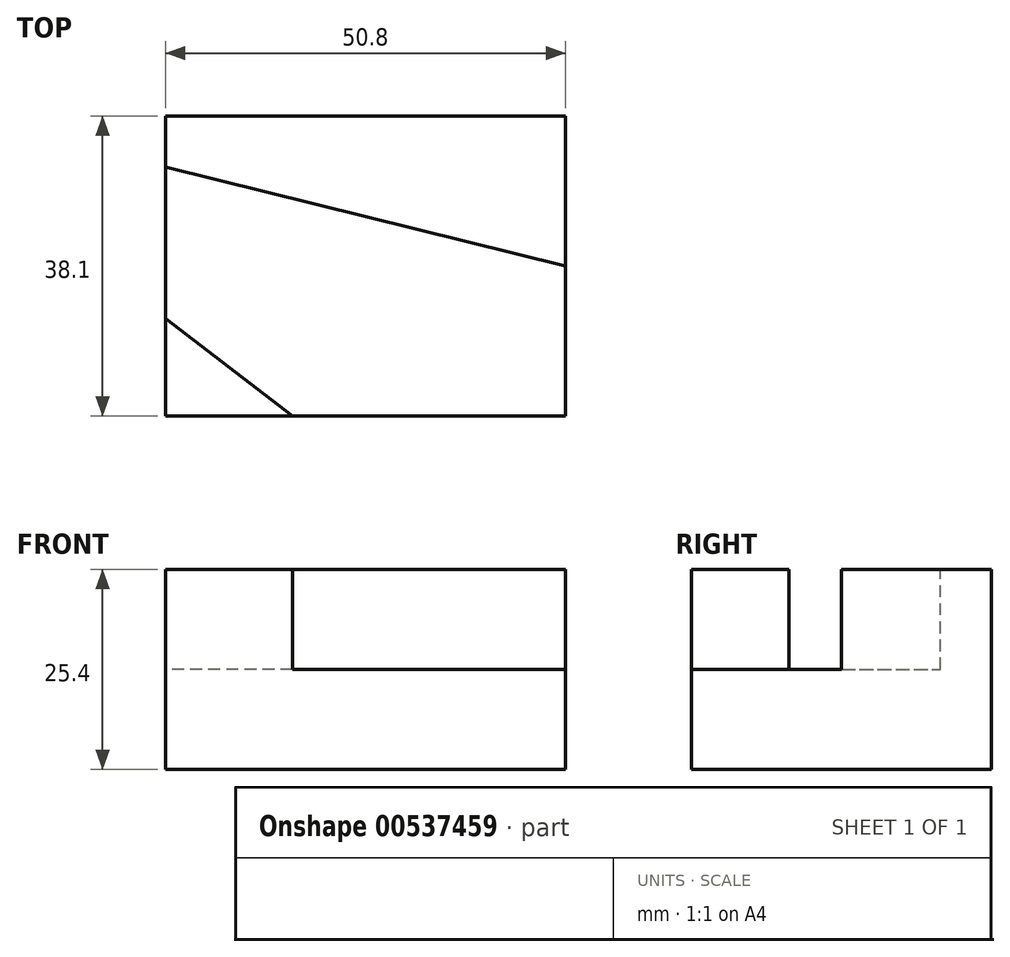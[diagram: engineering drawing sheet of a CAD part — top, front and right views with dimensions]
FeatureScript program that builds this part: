
annotation { "Feature Type Name" : "Feature", "Feature Type Description" : "" }
export const myFeature = defineFeature(function(context is Context, id is Id, definition is map)
    precondition{}
    {
        {
            var Q0;
            Q0=qCreatedBy(makeId("Right.planeOp"),FACE);
            var sketch = newSketch(context, id + "F0", { "sketchPlane" : qUnion([Q0])});
            skLineSegment(sketch, "E0", {"start": v(0, 0) * mm, "end": v(0, 25.4) * mm});
            skLineSegment(sketch, "E1", {"start": v(0, 25.4) * mm, "end": v(38.1, 25.4) * mm});
            skLineSegment(sketch, "E2", {"start": v(38.1, 25.4) * mm, "end": v(38.1, 0) * mm});
            skLineSegment(sketch, "E3", {"start": v(38.1, 0) * mm, "end": v(0, 0) * mm});
            skSolve(sketch);
        }
        {
            var Q0;
            Q0=makeQuery(id+"F0.imprint","IMPRINT",FACE,{"disambiguationData":[TD([[makeQuery(id+"F0.imprint","IMPRINT",EDGE,{"derivedFrom":sQuery(id+"F0.wireOp",EDGE,"E0")}),-1.0]])]});
            extrude(context, id + "F1", {"entities" : qUnion([Q0]), "depth" : 50.8 * mm, "offsetDistance" : 25.4 * mm});
        }
        {
            var Q0;
            Q0=makeQuery(id+"F1.opExtrude","SWEPT_FACE",FACE,{"disambiguationData":[OSD([sQuery(id+"F0.wireOp",EDGE,"E1")])]});
            var sketch = newSketch(context, id + "F2", { "sketchPlane" : qUnion([Q0])});
            skLineSegment(sketch, "E4", {"start": v(16.13, 0) * mm, "end": v(0, 12.4) * mm});
            skLineSegment(sketch, "E5", {"start": v(50.8, 19.05) * mm, "end": v(0, 31.63) * mm});
            skSolve(sketch);
        }
        {
            var Q0;
            Q0 = qSketchRegion(id + "F2", true);
            var Q1;
            {var subQ0=sQuery(id+"F2.wireOp",EDGE,"E4");Q1=makeQuery(id+"F2.imprint","IMPRINT",FACE,{"disambiguationData":[TD([[makeQuery(id+"F2.imprint","IMPRINT",EDGE,{"derivedFrom":subQ0}),-1.0]])]});}
            extrude(context, id + "F3", {"entities" : qUnion([Q0, Q1]), "operationType" : NewBodyOperationType.REMOVE, "oppositeDirection" : true, "depth" : 12.7 * mm, "offsetDistance" : 25.4 * mm});
        }
    });
